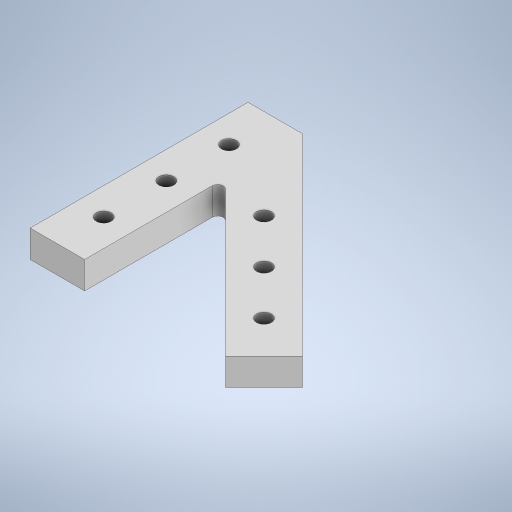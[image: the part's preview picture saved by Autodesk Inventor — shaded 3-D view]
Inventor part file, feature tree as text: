
AUTODESK INVENTOR PART (.ipt)
format: ipt  version: 2023 (Build 270158000, 158)  size: 264,192 bytes
history: native  units: mm
features: extrude x1, fillet x1, sketch x1
ambient origin geometry x8: Origin, YZ Plane, XZ Plane, XY Plane, X Axis, Y Axis, Z Axis, Center Point
bodies: Solid1 (feature_tree)
feature tree (3):
  extrude  "Extrusion1"  Depth=20.0mm
  fillet  "Fillet1"  Radius=100.0mm
  sketch  "Sketch2"  dims[d8=80.0mm d10=20.0mm d11=100.0mm d12=45.0deg d13=51.715729mm d14=28.284271mm d15=135.0deg d16=5.5118mm d18=30.0mm d20=23.0mm d21=10.0mm d23=10.0mm d26=30.0mm d28=23.0mm d29=10.0mm d31=10.0mm d33=80.0mm d34=10.0mm d35=17.0mm d36=10.0mm d37=17.0mm d38=10.0mm d39=0.0mm d46=2.0mm]
